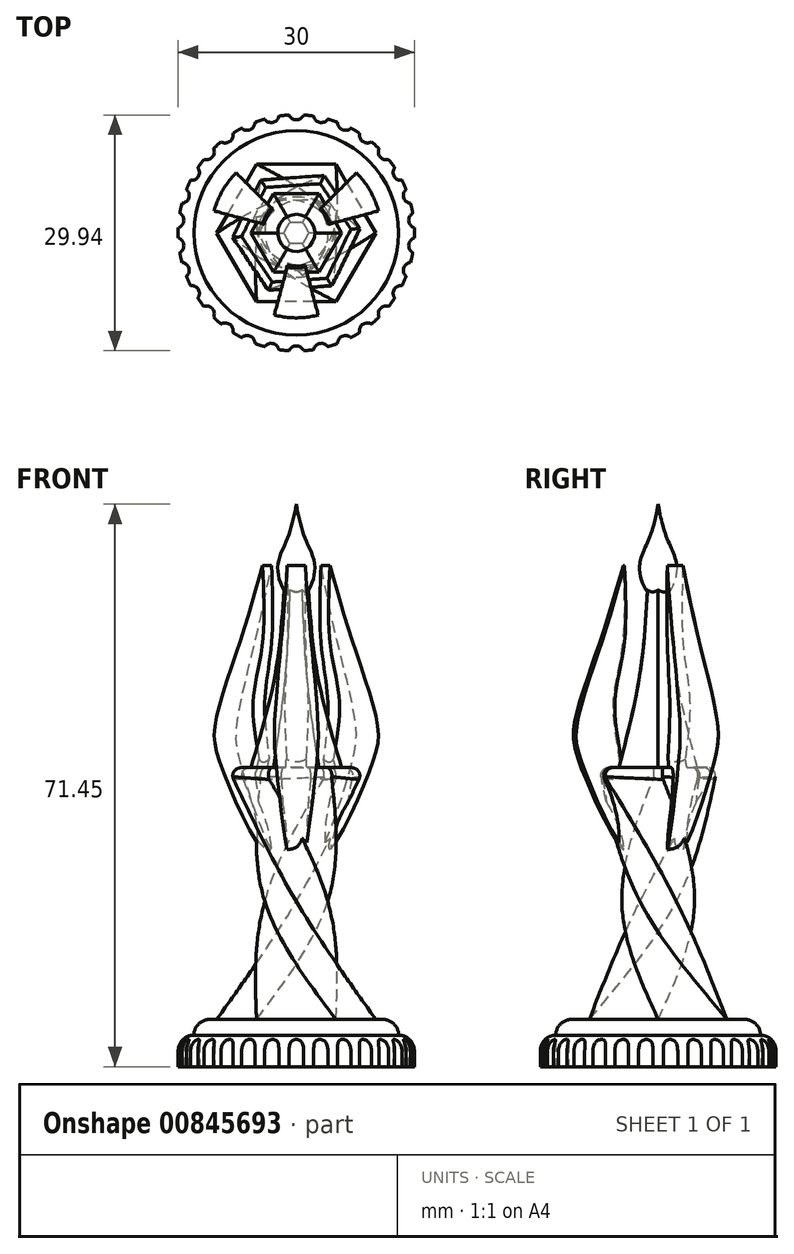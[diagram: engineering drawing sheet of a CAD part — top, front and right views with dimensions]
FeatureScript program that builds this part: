
annotation { "Feature Type Name" : "Feature", "Feature Type Description" : "" }
export const myFeature = defineFeature(function(context is Context, id is Id, definition is map)
    precondition{}
    {
        {
            var Q0;
            Q0=qCreatedBy(makeId("Top.planeOp"),FACE);
            var sketch = newSketch(context, id + "F0", { "sketchPlane" : qUnion([Q0])});
            skCircle(sketch, "E0", {"center": v(0, 0) * mm, "radius": 15 * mm});
            skSolve(sketch);
        }
        {
            var Q0;
            Q0=qSketchRegion(id+"F0",true);
            extrude(context, id + "F1", {"entities" : qUnion([Q0]), "depth" : 4 * mm, "offsetDistance" : 25 * mm});
        }
        {
            var Q0;
            Q0=makeQuery(id+"F1.opExtrude","CAP_FACE",FACE,{"disambiguationData":[OSD([sQuery(id+"F0.wireOp",EDGE,"E0")])],"isStart":false});
            var sketch = newSketch(context, id + "F2", { "sketchPlane" : qUnion([Q0])});
            skCircle(sketch, "E1", {"center": v(0, 0) * mm, "radius": 13 * mm});
            skSolve(sketch);
        }
        {
            var Q0;
            Q0=qSketchRegion(id+"F2",true);
            extrude(context, id + "F3", {"entities" : qUnion([Q0]), "operationType" : NewBodyOperationType.ADD, "depth" : 2 * mm, "offsetDistance" : 25 * mm});
        }
        {
            var Q0;
            Q0=makeQuery(id+"F1.opExtrude","CAP_EDGE",EDGE,{"disambiguationData":[OSD([sQuery(id+"F0.wireOp",EDGE,"E0")])],"isStart":false});
            var Q1;
            Q1=makeQuery(id+"F3.opExtrude","CAP_EDGE",EDGE,{"disambiguationData":[OSD([sQuery(id+"F2.wireOp",EDGE,"E1")])],"isStart":false});
            fillet(context, id + "F4", {"entities" : qUnion([Q0, Q1]), "radius" : 2 * mm, "tangentPropagation" : true, "allowEdgeOverflow" : false});
        }
        {
            var Q0;
            Q0=makeQuery(id+"F1.opExtrude","CAP_FACE",FACE,{"disambiguationData":[OSD([sQuery(id+"F0.wireOp",EDGE,"E0")])],"isStart":true});
            var sketch = newSketch(context, id + "F5", { "sketchPlane" : qUnion([Q0])});
            skCircle(sketch, "E2", {"center": v(0, 15.36) * mm, "radius": 1 * mm});
            skCircle(sketch, "E3.1.0", {"center": v(-3.2, 15.02) * mm, "radius": 1 * mm});
            skCircle(sketch, "E3.2.0", {"center": v(-6.25, 14.03) * mm, "radius": 1 * mm});
            skCircle(sketch, "E3.3.0", {"center": v(-9.03, 12.43) * mm, "radius": 1 * mm});
            skCircle(sketch, "E3.4.0", {"center": v(-11.41, 10.28) * mm, "radius": 1 * mm});
            skCircle(sketch, "E3.5.0", {"center": v(-13.3, 7.68) * mm, "radius": 1 * mm});
            skCircle(sketch, "E3.6.0", {"center": v(-14.6, 4.75) * mm, "radius": 1 * mm});
            skCircle(sketch, "E3.7.0", {"center": v(-15.27, 1.6) * mm, "radius": 1 * mm});
            skCircle(sketch, "E3.8.0", {"center": v(-15.27, -1.6) * mm, "radius": 1 * mm});
            skCircle(sketch, "E3.9.0", {"center": v(-14.6, -4.75) * mm, "radius": 1 * mm});
            skCircle(sketch, "E3.10.0", {"center": v(-13.3, -7.68) * mm, "radius": 1 * mm});
            skCircle(sketch, "E3.11.0", {"center": v(-11.41, -10.28) * mm, "radius": 1 * mm});
            skCircle(sketch, "E3.12.0", {"center": v(-9.03, -12.43) * mm, "radius": 1 * mm});
            skCircle(sketch, "E3.13.0", {"center": v(-6.25, -14.03) * mm, "radius": 1 * mm});
            skCircle(sketch, "E3.14.0", {"center": v(-3.2, -15.02) * mm, "radius": 1 * mm});
            skCircle(sketch, "E3.15.0", {"center": v(0, -15.36) * mm, "radius": 1 * mm});
            skCircle(sketch, "E3.16.0", {"center": v(3.2, -15.02) * mm, "radius": 1 * mm});
            skCircle(sketch, "E3.17.0", {"center": v(6.25, -14.03) * mm, "radius": 1 * mm});
            skCircle(sketch, "E3.18.0", {"center": v(9.03, -12.43) * mm, "radius": 1 * mm});
            skCircle(sketch, "E3.19.0", {"center": v(11.41, -10.28) * mm, "radius": 1 * mm});
            skCircle(sketch, "E3.20.0", {"center": v(13.3, -7.68) * mm, "radius": 1 * mm});
            skCircle(sketch, "E3.21.0", {"center": v(14.6, -4.75) * mm, "radius": 1 * mm});
            skCircle(sketch, "E3.22.0", {"center": v(15.27, -1.6) * mm, "radius": 1 * mm});
            skCircle(sketch, "E3.23.0", {"center": v(15.27, 1.6) * mm, "radius": 1 * mm});
            skCircle(sketch, "E3.24.0", {"center": v(14.6, 4.75) * mm, "radius": 1 * mm});
            skCircle(sketch, "E3.25.0", {"center": v(13.3, 7.68) * mm, "radius": 1 * mm});
            skCircle(sketch, "E3.26.0", {"center": v(11.41, 10.28) * mm, "radius": 1 * mm});
            skCircle(sketch, "E3.27.0", {"center": v(9.03, 12.43) * mm, "radius": 1 * mm});
            skCircle(sketch, "E3.28.0", {"center": v(6.25, 14.03) * mm, "radius": 1 * mm});
            skCircle(sketch, "E3.29.0", {"center": v(3.2, 15.02) * mm, "radius": 1 * mm});
            skPoint(sketch, "E3.center", {"position": v(0, 0) * mm});
            skSolve(sketch);
        }
        {
            var Q0;
            Q0=qSketchRegion(id+"F5",true);
            extrude(context, id + "F6", {"entities" : qUnion([Q0]), "operationType" : NewBodyOperationType.REMOVE, "oppositeDirection" : true, "depth" : 25 * mm, "offsetDistance" : 25 * mm});
        }
        {
            var Q0;
            Q0=makeQuery(id+"F3.opExtrude","CAP_FACE",FACE,{"disambiguationData":[OSD([sQuery(id+"F2.wireOp",EDGE,"E1")])],"isStart":false});
            var sketch = newSketch(context, id + "F7", { "sketchPlane" : qUnion([Q0])});
            skCircle(sketch, "E4.cCircle", {"center": v(0, 0) * mm, "radius": 8.75 * mm, "construction": true});
            skLineSegment(sketch, "E4.0", {"start": v(10.1, 0) * mm, "end": v(5.05, -8.75) * mm});
            skLineSegment(sketch, "E4.1", {"start": v(5.05, -8.75) * mm, "end": v(-5.05, -8.75) * mm});
            skLineSegment(sketch, "E4.2", {"start": v(-5.05, -8.75) * mm, "end": v(-10.1, 0) * mm});
            skLineSegment(sketch, "E4.3", {"start": v(-10.1, 0) * mm, "end": v(-5.05, 8.75) * mm});
            skLineSegment(sketch, "E4.4", {"start": v(-5.05, 8.75) * mm, "end": v(5.05, 8.75) * mm});
            skLineSegment(sketch, "E4.5", {"start": v(5.05, 8.75) * mm, "end": v(10.1, 0) * mm});
            skPoint(sketch, "E4.0.midPoint", {"position": v(7.58, -4.38) * mm});
            skSolve(sketch);
        }
        {
            var Q0;
            Q0=qCreatedBy(makeId("Front.planeOp"),FACE);
            var sketch = newSketch(context, id + "F8", { "sketchPlane" : qUnion([Q0])});
            skLineSegment(sketch, "E5", {"start": v(0, 0) * mm, "end": v(0, 62.44) * mm, "construction": true});
            skSolve(sketch);
        }
        {
            var Q0;
            Q0=makeQuery(id+"F7.imprint","IMPRINT",FACE,{"disambiguationData":[TD([[makeQuery(id+"F7.imprint","IMPRINT",EDGE,{"derivedFrom":sQuery(id+"F7.wireOp",EDGE,"E4.0")}),-1.0]])]});
            cPlane(context, id + "F9", {"entities" : qUnion([Q0]), "cplaneType" : CPlaneType.OFFSET, "offset" : 32 * mm, "width" : 150 * mm, "height" : 150 * mm});
        }
        {
            var Q0;
            Q0=qCreatedBy(id+"F9.planeOp",FACE);
            var sketch = newSketch(context, id + "F10", { "sketchPlane" : qUnion([Q0])});
            skCircle(sketch, "E6.cCircle", {"center": v(0, 0) * mm, "radius": 5 * mm, "construction": true});
            skLineSegment(sketch, "E6.0", {"start": v(2.89, -5) * mm, "end": v(-2.89, -5) * mm});
            skLineSegment(sketch, "E6.1", {"start": v(-2.89, -5) * mm, "end": v(-5.77, 0) * mm});
            skLineSegment(sketch, "E6.2", {"start": v(-5.77, 0) * mm, "end": v(-2.89, 5) * mm});
            skLineSegment(sketch, "E6.3", {"start": v(-2.89, 5) * mm, "end": v(2.89, 5) * mm});
            skLineSegment(sketch, "E6.4", {"start": v(2.89, 5) * mm, "end": v(5.77, 0) * mm});
            skLineSegment(sketch, "E6.5", {"start": v(5.77, 0) * mm, "end": v(2.89, -5) * mm});
            skPoint(sketch, "E6.0.midPoint", {"position": v(0, -5) * mm});
            skSolve(sketch);
        }
        {
            var Q0;
            Q0=qCreatedBy(id+"F9.planeOp",FACE);
            cPlane(context, id + "F11", {"entities" : qUnion([Q0]), "cplaneType" : CPlaneType.OFFSET, "offset" : 12 * mm, "width" : 150 * mm, "height" : 150 * mm});
        }
        {
            var Q0;
            Q0=qCreatedBy(id+"F11.planeOp",FACE);
            cPlane(context, id + "F12", {"entities" : qUnion([Q0]), "cplaneType" : CPlaneType.OFFSET, "offset" : 12 * mm, "width" : 150 * mm, "height" : 150 * mm});
        }
        {
            var Q0;
            Q0=qCreatedBy(id+"F11.planeOp",FACE);
            var sketch = newSketch(context, id + "F13", { "sketchPlane" : qUnion([Q0])});
            skCircle(sketch, "E7.cCircle", {"center": v(0, 0) * mm, "radius": 2.3 * mm, "construction": true});
            skLineSegment(sketch, "E7.0", {"start": v(1.33, -2.3) * mm, "end": v(-1.33, -2.3) * mm});
            skLineSegment(sketch, "E7.1", {"start": v(-1.33, -2.3) * mm, "end": v(-2.66, 0) * mm});
            skLineSegment(sketch, "E7.2", {"start": v(-2.66, 0) * mm, "end": v(-1.33, 2.3) * mm});
            skLineSegment(sketch, "E7.3", {"start": v(-1.33, 2.3) * mm, "end": v(1.33, 2.3) * mm});
            skLineSegment(sketch, "E7.4", {"start": v(1.33, 2.3) * mm, "end": v(2.66, 0) * mm});
            skLineSegment(sketch, "E7.5", {"start": v(2.66, 0) * mm, "end": v(1.33, -2.3) * mm});
            skPoint(sketch, "E7.0.midPoint", {"position": v(0, -2.3) * mm});
            skSolve(sketch);
        }
        {
            var Q0;
            Q0=qCreatedBy(id+"F12.planeOp",FACE);
            var sketch = newSketch(context, id + "F14", { "sketchPlane" : qUnion([Q0])});
            skCircle(sketch, "E8.cCircle", {"center": v(0, 0) * mm, "radius": 1.3 * mm, "construction": true});
            skLineSegment(sketch, "E8.0", {"start": v(0.75, -1.3) * mm, "end": v(-0.75, -1.3) * mm});
            skLineSegment(sketch, "E8.1", {"start": v(-0.75, -1.3) * mm, "end": v(-1.5, 0) * mm});
            skLineSegment(sketch, "E8.2", {"start": v(-1.5, 0) * mm, "end": v(-0.75, 1.3) * mm});
            skLineSegment(sketch, "E8.3", {"start": v(-0.75, 1.3) * mm, "end": v(0.75, 1.3) * mm});
            skLineSegment(sketch, "E8.4", {"start": v(0.75, 1.3) * mm, "end": v(1.5, 0) * mm});
            skLineSegment(sketch, "E8.5", {"start": v(1.5, 0) * mm, "end": v(0.75, -1.3) * mm});
            skPoint(sketch, "E8.0.midPoint", {"position": v(0, -1.3) * mm});
            skSolve(sketch);
        }
        {
            var Q1;
            Q1=makeQuery(id+"F10.imprint","IMPRINT",FACE,{"disambiguationData":[TD([[makeQuery(id+"F10.imprint","IMPRINT",EDGE,{"derivedFrom":sQuery(id+"F10.wireOp",EDGE,"E6.0")}),-1.0]])]});
            var Q2;
            Q2=makeQuery(id+"F13.imprint","IMPRINT",FACE,{"disambiguationData":[TD([[makeQuery(id+"F13.imprint","IMPRINT",EDGE,{"derivedFrom":sQuery(id+"F13.wireOp",EDGE,"E7.0")}),-1.0]])]});
            var Q3;
            Q3=makeQuery(id+"F14.imprint","IMPRINT",FACE,{"disambiguationData":[TD([[makeQuery(id+"F14.imprint","IMPRINT",EDGE,{"derivedFrom":sQuery(id+"F14.wireOp",EDGE,"E8.0")}),-1.0]])]});
            loft(context, id + "F15", {"operationType" : NewBodyOperationType.ADD, "sheetProfilesArray" : [{ "sheetProfileEntities" : qUnion([Q1]) }, { "sheetProfileEntities" : qUnion([Q2]) }, { "sheetProfileEntities" : qUnion([Q3]) }]});
        }
        {
            var Q0;
            Q0=qCreatedBy(makeId("Right.planeOp"),FACE);
            var sketch = newSketch(context, id + "F16", { "sketchPlane" : qUnion([Q0])});
            skFitSpline(sketch, "E9", {"points": [v(0, 71.45) * mm, v(1.2, 66.94) * mm, v(2.36, 63.44) * mm, v(1.22, 60.12) * mm, v(0, 59.63) * mm], "startDerivative": vector(3, -17.34) * mm, "endDerivative": vector(-7.74, -0.13) * mm});
            skLineSegment(sketch, "E10", {"start": v(0, 71.45) * mm, "end": v(0, 59.63) * mm});
            skSolve(sketch);
        }
        {
            var Q0;
            Q0 = qSketchRegion(id + "F16", true);
            var Q1;
            Q1=sQuery(id+"F8.wireOp",EDGE,"E5");
            revolve(context, id + "F17", {"operationType" : NewBodyOperationType.ADD, "surfaceOperationType" : NewSurfaceOperationType.NEW, "entities" : qUnion([Q0]), "axis" : qUnion([Q1]), "revolveType" : RevolveType.FULL});
        }
        {
            var Q0;
            Q0=qCreatedBy(makeId("Right.planeOp"),FACE);
            var sketch = newSketch(context, id + "F18", { "sketchPlane" : qUnion([Q0])});
            skFitSpline(sketch, "E11", {"points": [v(-3.78, 26.78) * mm, v(-9.85, 38.17) * mm, v(-10.7, 43.34) * mm, v(-7.61, 53.32) * mm, v(-4.44, 63.64) * mm], "startDerivative": vector(-21.08, 19.73) * mm, "endDerivative": vector(10.73, 38.3) * mm});
            skFitSpline(sketch, "E12", {"points": [v(-4.44, 63.64) * mm, v(-4.44, 53.94) * mm, v(-5.55, 47.62) * mm, v(-5.39, 42.2) * mm, v(-3.58, 30.64) * mm, v(-3.78, 26.78) * mm], "startDerivative": vector(2.4, -43.83) * mm, "endDerivative": vector(-5.04, -27.17) * mm});
            skSolve(sketch);
        }
        {
            var Q0;
            Q0 = qSketchRegion(id + "F18", true);
            var Q1;
            Q1=sQuery(id+"F8.wireOp",EDGE,"E5");
            revolve(context, id + "F19", {"surfaceOperationType" : NewSurfaceOperationType.NEW, "entities" : qUnion([Q0]), "axis" : qUnion([Q1]), "revolveType" : RevolveType.SYMMETRIC, "angle" : 30 * degree});
        }
        {
            var Q0;
            Q0=makeQuery(id+"F19.opRevolve","SWEPT_BODY",BODY,{"disambiguationData":[OSD([sQuery(id+"F18.wireOp",EDGE,"E11"),sQuery(id+"F18.wireOp",EDGE,"E12")])]});
            var Q1;
            Q1=sQuery(id+"F8.wireOp",EDGE,"E5");
            circularPattern(context, id + "F20", {"entities" : qUnion([Q0]), "axis" : qUnion([Q1]), "angle" : 360 * degree, "instanceCount" : 3, "equalSpace" : true});
        }
        {
            var Q0;
            Q0=makeQuery(id+"F3.opExtrude","CAP_FACE",FACE,{"disambiguationData":[OSD([sQuery(id+"F2.wireOp",EDGE,"E1")])],"isStart":false});
            cPlane(context, id + "F21", {"entities" : qUnion([Q0]), "cplaneType" : CPlaneType.OFFSET, "offset" : 32 * mm, "width" : 150 * mm, "height" : 150 * mm});
        }
        {
            var Q0;
            Q0=qCreatedBy(id+"F21.planeOp",FACE);
            var sketch = newSketch(context, id + "F22", { "sketchPlane" : qUnion([Q0])});
            skCircle(sketch, "E13.cCircle", {"center": v(0, 0) * mm, "radius": 7.5 * mm, "construction": true});
            skLineSegment(sketch, "E13.0", {"start": v(-4.33, 7.5) * mm, "end": v(4.33, 7.5) * mm});
            skLineSegment(sketch, "E13.1", {"start": v(4.33, 7.5) * mm, "end": v(8.66, 0) * mm});
            skLineSegment(sketch, "E13.2", {"start": v(8.66, 0) * mm, "end": v(4.33, -7.5) * mm});
            skLineSegment(sketch, "E13.3", {"start": v(4.33, -7.5) * mm, "end": v(-4.33, -7.5) * mm});
            skLineSegment(sketch, "E13.4", {"start": v(-4.33, -7.5) * mm, "end": v(-8.66, 0) * mm});
            skLineSegment(sketch, "E13.5", {"start": v(-8.66, 0) * mm, "end": v(-4.33, 7.5) * mm});
            skPoint(sketch, "E13.0.midPoint", {"position": v(0, 7.5) * mm});
            skSolve(sketch);
        }
        {
            var Q0;
            Q0=makeQuery(id+"F7.imprint","IMPRINT",FACE,{"disambiguationData":[TD([[makeQuery(id+"F7.imprint","IMPRINT",EDGE,{"derivedFrom":sQuery(id+"F7.wireOp",EDGE,"E4.0")}),1.0]])]});
            cPlane(context, id + "F23", {"entities" : qUnion([Q0]), "cplaneType" : CPlaneType.OFFSET, "offset" : 15 * mm, "width" : 150 * mm, "height" : 150 * mm});
        }
        {
            var Q0;
            Q0=qCreatedBy(id+"F23.planeOp",FACE);
            var sketch = newSketch(context, id + "F24", { "sketchPlane" : qUnion([Q0])});
            skCircle(sketch, "E14.cCircle", {"center": v(0, 0) * mm, "radius": 4 * mm, "construction": true});
            skLineSegment(sketch, "E14.0", {"start": v(4, 2.3) * mm, "end": v(4, -2.3) * mm});
            skLineSegment(sketch, "E14.1", {"start": v(4, -2.3) * mm, "end": v(0, -4.62) * mm});
            skLineSegment(sketch, "E14.2", {"start": v(0, -4.62) * mm, "end": v(-4, -2.3) * mm});
            skLineSegment(sketch, "E14.3", {"start": v(-4, -2.3) * mm, "end": v(-4, 2.3) * mm});
            skLineSegment(sketch, "E14.4", {"start": v(-4, 2.3) * mm, "end": v(0, 4.62) * mm});
            skLineSegment(sketch, "E14.5", {"start": v(0, 4.62) * mm, "end": v(4, 2.3) * mm});
            skPoint(sketch, "E14.0.midPoint", {"position": v(4, 0) * mm});
            skSolve(sketch);
        }
        {
            var Q0;
            Q0=makeQuery(id+"F7.imprint","IMPRINT",FACE,{"disambiguationData":[TD([[makeQuery(id+"F7.imprint","IMPRINT",EDGE,{"derivedFrom":sQuery(id+"F7.wireOp",EDGE,"E4.0")}),-1.0]])]});
            var Q1;
            Q1=makeQuery(id+"F24.imprint","IMPRINT",FACE,{"disambiguationData":[TD([[makeQuery(id+"F24.imprint","IMPRINT",EDGE,{"derivedFrom":sQuery(id+"F24.wireOp",EDGE,"E14.0")}),-1.0]])]});
            var Q2;
            Q2=makeQuery(id+"F22.imprint","IMPRINT",FACE,{"disambiguationData":[TD([[makeQuery(id+"F22.imprint","IMPRINT",EDGE,{"derivedFrom":sQuery(id+"F22.wireOp",EDGE,"E13.0")}),-1.0]])]});
            var Q3;
            Q3=sQuery(id+"F7.wireOp",VERTEX,"E4.2.end");
            var Q4;
            Q4=sQuery(id+"F24.wireOp",VERTEX,"E14.4.end");
            var Q5;
            Q5=sQuery(id+"F22.wireOp",VERTEX,"E13.1.end");
            loft(context, id + "F25", {"sheetProfilesArray" : [{ "sheetProfileEntities" : qUnion([Q0]) }, { "sheetProfileEntities" : qUnion([Q1]) }, { "sheetProfileEntities" : qUnion([Q2]) }], "matchConnections" : true, "connections" : [{ "connectionEntities" : qUnion([Q3, Q4, Q5]), "connectionEdgeQueries" : qUnion([]), "connectionEdgeParameters" : [] }]});
        }
        {
            var Q0;
            Q0=makeQuery(id+"F15.opLoft","SWEPT_BODY",BODY,{"disambiguationData":[OSD([makeQuery(id+"F10.imprint","IMPRINT",FACE,{"disambiguationData":[TD([[makeQuery(id+"F10.imprint","IMPRINT",EDGE,{"derivedFrom":sQuery(id+"F10.wireOp",EDGE,"E6.0")}),-1.0]])]}),sQuery(id+"F13.wireOp",EDGE,"E7.5"),makeQuery(id+"F14.imprint","IMPRINT",FACE,{"disambiguationData":[TD([[makeQuery(id+"F14.imprint","IMPRINT",EDGE,{"derivedFrom":sQuery(id+"F14.wireOp",EDGE,"E8.0")}),-1.0]])]})])]});
            var Q1;
            Q1=makeQuery(id+"F1.opExtrude","SWEPT_BODY",BODY,{"disambiguationData":[OSD([sQuery(id+"F0.wireOp",EDGE,"E0")])]});
            var Q2;
            Q2=makeQuery(id+"F17.opRevolve","SWEPT_BODY",BODY,{"disambiguationData":[OSD([sQuery(id+"F16.wireOp",EDGE,"E9"),sQuery(id+"F16.wireOp",EDGE,"E10")])]});
            var Q3;
            Q3=makeQuery(id+"F19.opRevolve","SWEPT_BODY",BODY,{"disambiguationData":[OSD([sQuery(id+"F18.wireOp",EDGE,"E11"),sQuery(id+"F18.wireOp",EDGE,"E12")])]});
            var Q4;
            Q4=makeQuery(id+"F20.opPattern","COPY",BODY,{"derivedFrom":makeQuery(id+"F19.opRevolve","SWEPT_BODY",BODY,{"disambiguationData":[OSD([sQuery(id+"F18.wireOp",EDGE,"E11"),sQuery(id+"F18.wireOp",EDGE,"E12")])]}),"instanceName":"1"});
            var Q5;
            Q5=makeQuery(id+"F20.opPattern","COPY",BODY,{"derivedFrom":makeQuery(id+"F19.opRevolve","SWEPT_BODY",BODY,{"disambiguationData":[OSD([sQuery(id+"F18.wireOp",EDGE,"E11"),sQuery(id+"F18.wireOp",EDGE,"E12")])]}),"instanceName":"2"});
            var Q6;
            Q6=makeQuery(id+"F25.opLoft","SWEPT_BODY",BODY,{"disambiguationData":[OSD([makeQuery(id+"F7.imprint","IMPRINT",FACE,{"disambiguationData":[TD([[makeQuery(id+"F7.imprint","IMPRINT",EDGE,{"derivedFrom":sQuery(id+"F7.wireOp",EDGE,"E4.0")}),-1.0]])]}),makeQuery(id+"F22.imprint","IMPRINT",FACE,{"disambiguationData":[TD([[makeQuery(id+"F22.imprint","IMPRINT",EDGE,{"derivedFrom":sQuery(id+"F22.wireOp",EDGE,"E13.0")}),-1.0]])]}),sQuery(id+"F24.wireOp",EDGE,"E14.5")])]});
            booleanBodies(context, id + "F26", {"operationType" : BooleanOperationType.UNION, "tools" : qUnion([Q0, Q1, Q2, Q3, Q4, Q5, Q6])});
        }
        {
            var Q0;
            Q0=makeQuery(id+"F25.opLoft","MID_CAP_EDGE",EDGE,{"disambiguationData":[OSD([sQuery(id+"F22.wireOp",EDGE,"E13.1"),sQuery(id+"F22.wireOp",EDGE,"E13.2"),sQuery(id+"F22.wireOp",EDGE,"E13.3")])],"capPos":2.0});
            var Q1;
            {var subQ2=sQuery(id+"F22.wireOp",EDGE,"E13.3");var subQ3=sQuery(id+"F22.wireOp",EDGE,"E13.2");var subQ7=sQuery(id+"F22.wireOp",EDGE,"E13.4");Q1=makeQuery(id+"F26.opBoolean","SPLIT",EDGE,{"disambiguationData":[TD([makeQuery(id+"F19.opRevolve","CAP_FACE",FACE,{"disambiguationData":[OSD([sQuery(id+"F18.wireOp",EDGE,"E11"),sQuery(id+"F18.wireOp",EDGE,"E12")])],"isStart":false})])],"derivedFrom":makeQuery(id+"F25.opLoft","MID_CAP_EDGE",EDGE,{"disambiguationData":[OSD([subQ3,subQ2,subQ7])],"capPos":2.0})});}
            var Q2;
            {var subQ3=sQuery(id+"F22.wireOp",EDGE,"E13.2");var subQ4=sQuery(id+"F22.wireOp",EDGE,"E13.1");var subQ7=sQuery(id+"F22.wireOp",EDGE,"E13.0");Q2=makeQuery(id+"F26.opBoolean","SPLIT",EDGE,{"disambiguationData":[TD([makeQuery(id+"F20.opPattern","COPY",FACE,{"derivedFrom":makeQuery(id+"F19.opRevolve","CAP_FACE",FACE,{"disambiguationData":[OSD([sQuery(id+"F18.wireOp",EDGE,"E11"),sQuery(id+"F18.wireOp",EDGE,"E12")])],"isStart":true}),"instanceName":"1"})])],"derivedFrom":makeQuery(id+"F25.opLoft","MID_CAP_EDGE",EDGE,{"disambiguationData":[OSD([subQ7,subQ4,subQ3])],"capPos":2.0})});}
            var Q3;
            {var subQ3=sQuery(id+"F22.wireOp",EDGE,"E13.4");var subQ4=sQuery(id+"F22.wireOp",EDGE,"E13.3");var subQ7=sQuery(id+"F22.wireOp",EDGE,"E13.2");Q3=makeQuery(id+"F26.opBoolean","SPLIT",EDGE,{"disambiguationData":[TD([makeQuery(id+"F19.opRevolve","CAP_FACE",FACE,{"disambiguationData":[OSD([sQuery(id+"F18.wireOp",EDGE,"E11"),sQuery(id+"F18.wireOp",EDGE,"E12")])],"isStart":true})])],"derivedFrom":makeQuery(id+"F25.opLoft","MID_CAP_EDGE",EDGE,{"disambiguationData":[OSD([subQ7,subQ4,subQ3])],"capPos":2.0})});}
            var Q4;
            Q4=makeQuery(id+"F25.opLoft","MID_CAP_EDGE",EDGE,{"disambiguationData":[OSD([sQuery(id+"F22.wireOp",EDGE,"E13.3"),sQuery(id+"F22.wireOp",EDGE,"E13.4"),sQuery(id+"F22.wireOp",EDGE,"E13.5")])],"capPos":2.0});
            var Q5;
            {var subQ2=sQuery(id+"F22.wireOp",EDGE,"E13.5");var subQ3=sQuery(id+"F22.wireOp",EDGE,"E13.4");var subQ4=sQuery(id+"F22.wireOp",EDGE,"E13.0");Q5=makeQuery(id+"F26.opBoolean","SPLIT",EDGE,{"disambiguationData":[TD([makeQuery(id+"F20.opPattern","COPY",FACE,{"derivedFrom":makeQuery(id+"F19.opRevolve","CAP_FACE",FACE,{"disambiguationData":[OSD([sQuery(id+"F18.wireOp",EDGE,"E11"),sQuery(id+"F18.wireOp",EDGE,"E12")])],"isStart":false}),"instanceName":"2"})])],"derivedFrom":makeQuery(id+"F25.opLoft","MID_CAP_EDGE",EDGE,{"disambiguationData":[OSD([subQ4,subQ3,subQ2])],"capPos":2.0})});}
            var Q6;
            {var subQ2=sQuery(id+"F22.wireOp",EDGE,"E13.5");var subQ3=sQuery(id+"F22.wireOp",EDGE,"E13.4");var subQ4=sQuery(id+"F22.wireOp",EDGE,"E13.0");Q6=makeQuery(id+"F26.opBoolean","SPLIT",EDGE,{"disambiguationData":[TD([makeQuery(id+"F20.opPattern","COPY",FACE,{"derivedFrom":makeQuery(id+"F19.opRevolve","CAP_FACE",FACE,{"disambiguationData":[OSD([sQuery(id+"F18.wireOp",EDGE,"E11"),sQuery(id+"F18.wireOp",EDGE,"E12")])],"isStart":true}),"instanceName":"2"})])],"derivedFrom":makeQuery(id+"F25.opLoft","MID_CAP_EDGE",EDGE,{"disambiguationData":[OSD([subQ4,subQ3,subQ2])],"capPos":2.0})});}
            var Q7;
            Q7=makeQuery(id+"F25.opLoft","MID_CAP_EDGE",EDGE,{"disambiguationData":[OSD([sQuery(id+"F22.wireOp",EDGE,"E13.0"),sQuery(id+"F22.wireOp",EDGE,"E13.1"),sQuery(id+"F22.wireOp",EDGE,"E13.5")])],"capPos":2.0});
            var Q8;
            {var subQ3=sQuery(id+"F22.wireOp",EDGE,"E13.1");var subQ4=sQuery(id+"F22.wireOp",EDGE,"E13.0");var subQ7=sQuery(id+"F22.wireOp",EDGE,"E13.2");Q8=makeQuery(id+"F26.opBoolean","SPLIT",EDGE,{"disambiguationData":[TD([makeQuery(id+"F20.opPattern","COPY",FACE,{"derivedFrom":makeQuery(id+"F19.opRevolve","CAP_FACE",FACE,{"disambiguationData":[OSD([sQuery(id+"F18.wireOp",EDGE,"E11"),sQuery(id+"F18.wireOp",EDGE,"E12")])],"isStart":false}),"instanceName":"1"})])],"derivedFrom":makeQuery(id+"F25.opLoft","MID_CAP_EDGE",EDGE,{"disambiguationData":[OSD([subQ4,subQ3,subQ7])],"capPos":2.0})});}
            fillet(context, id + "F27", {"entities" : qUnion([Q0, Q1, Q2, Q3, Q4, Q5, Q6, Q7, Q8]), "radius" : 1 * mm, "tangentPropagation" : true, "allowEdgeOverflow" : false});
        }
    });
